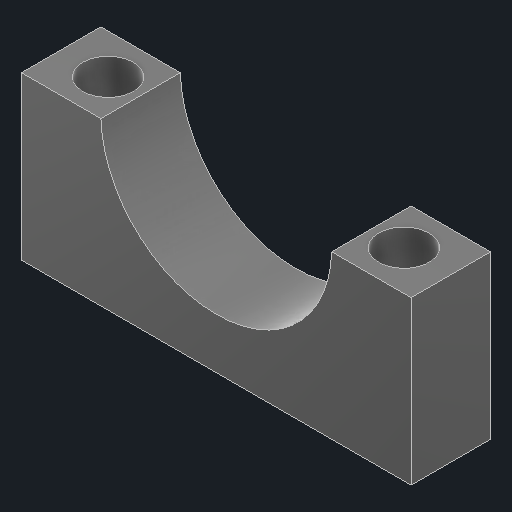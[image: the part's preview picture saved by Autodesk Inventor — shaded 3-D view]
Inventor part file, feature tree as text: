
AUTODESK INVENTOR PART (.ipt)
format: ipt  version: 2025 (Build 290162010, 162A)  size: 128,000 bytes
history: native  units: mm
features: extrude x2
ambient origin geometry x8: Origin, YZ Plane, XZ Plane, XY Plane, X Axis, Y Axis, Z Axis, Center Point
bodies: Solid1 (feature_tree)
feature tree (2):
  extrude  "Extrusion1"  Depth=16.0mm
  extrude  "Extrusion2"  Depth=27.0mm
